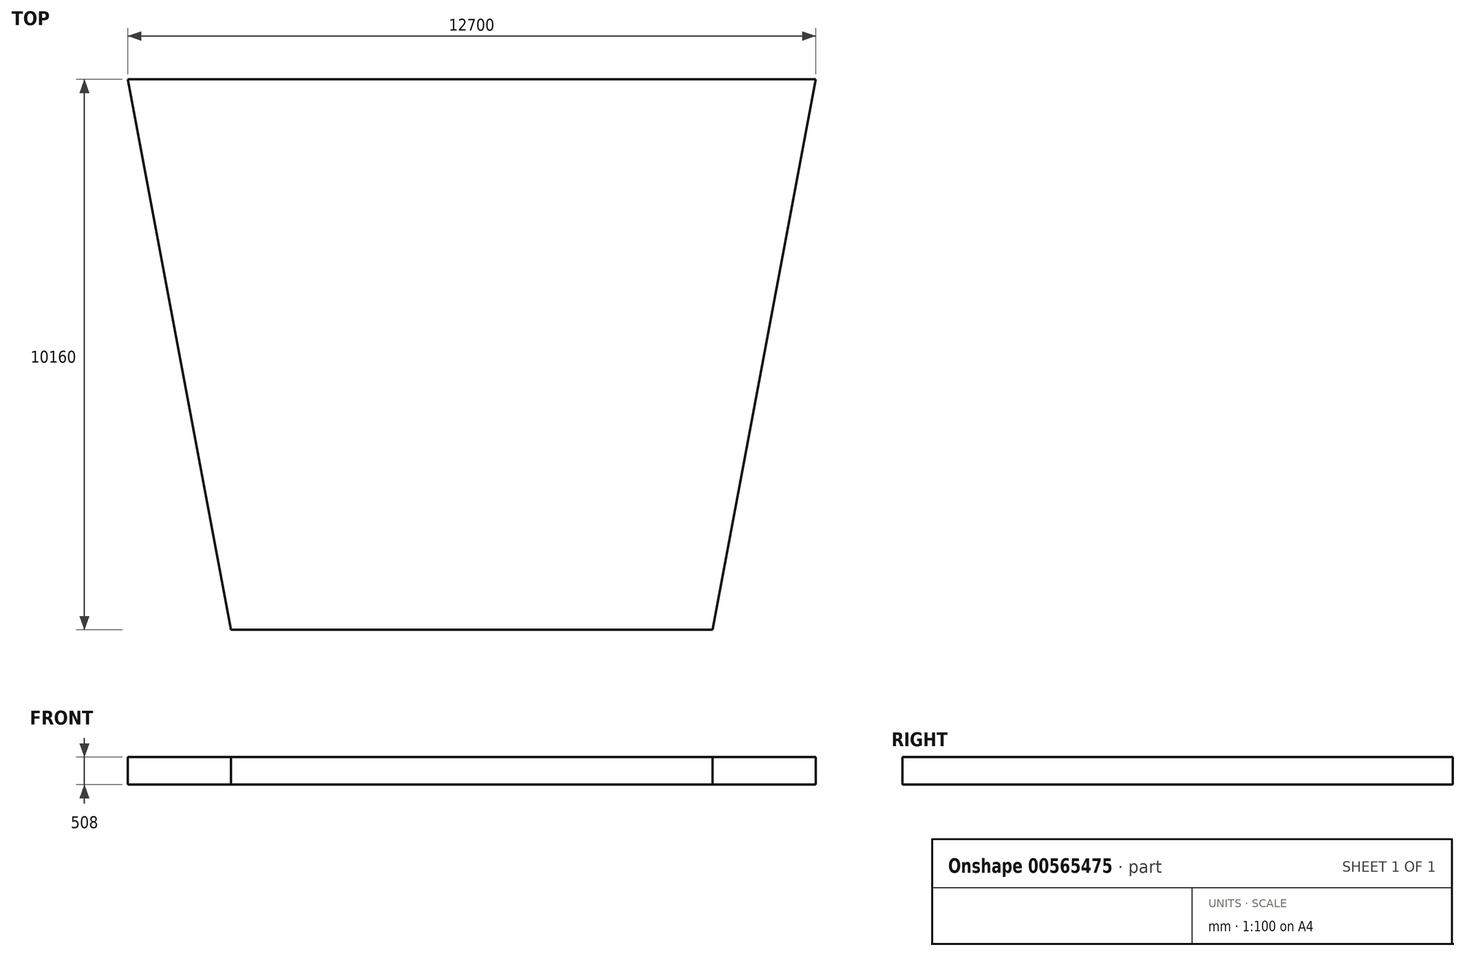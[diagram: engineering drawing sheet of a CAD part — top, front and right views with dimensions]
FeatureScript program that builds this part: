
annotation { "Feature Type Name" : "Feature", "Feature Type Description" : "" }
export const myFeature = defineFeature(function(context is Context, id is Id, definition is map)
    precondition{}
    {
        {
            var Q0;
            Q0=qCreatedBy(makeId("Top.planeOp"),FACE);
            var sketch = newSketch(context, id + "F0", { "sketchPlane" : qUnion([Q0])});
            skLineSegment(sketch, "E0", {"start": v(-4445, 0) * mm, "end": v(4445, 0) * mm});
            skLineSegment(sketch, "E1", {"start": v(4445, 0) * mm, "end": v(6350, 10160) * mm});
            skLineSegment(sketch, "E2", {"start": v(6350, 10160) * mm, "end": v(-6350, 10160) * mm});
            skLineSegment(sketch, "E3", {"start": v(-6350, 10160) * mm, "end": v(-4445, 0) * mm});
            skSolve(sketch);
        }
        {
            var Q0;
            Q0=makeQuery(id+"F0.imprint","IMPRINT",FACE,{"disambiguationData":[TD([[makeQuery(id+"F0.imprint","IMPRINT",EDGE,{"derivedFrom":sQuery(id+"F0.wireOp",EDGE,"E0")}),1.0]])]});
            extrude(context, id + "F1", {"entities" : qUnion([Q0]), "depth" : 508 * mm, "offsetDistance" : 25.4 * mm});
        }
    });
